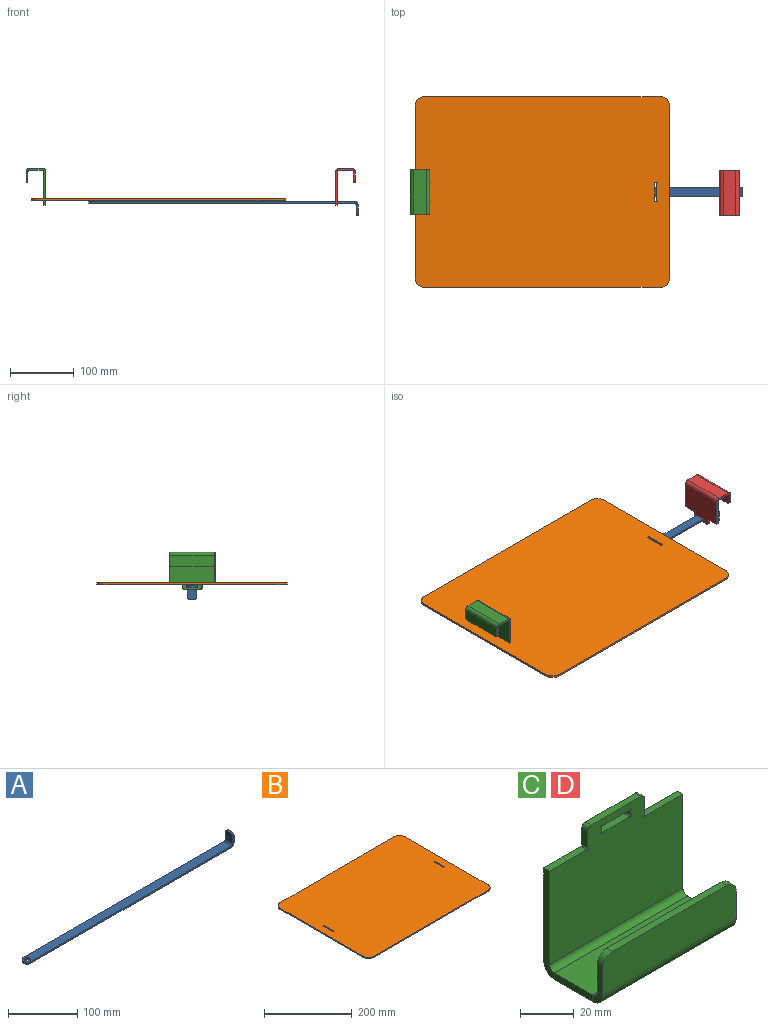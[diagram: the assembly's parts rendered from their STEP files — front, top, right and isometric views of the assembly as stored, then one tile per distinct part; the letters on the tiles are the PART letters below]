
ASSEMBLY  parts=4 mates=6
PART A: 19 faces, bbox 423x15x23 mm
  f0: plane 410.5x3mm, normal (0,1,0), area 1231.5mm2, adj f4,f5,f7,f16
  f1: plane 410.5x3mm, normal (0,-1,0), area 1231.5mm2, adj f4,f5,f6,f15
  f2: cylinder r=4.5mm len=9mm, axis (0,0,-1), area 84.8mm2, adj f4,f5
  f3: plane 3x1mm, normal (-1,0,0), area 3mm2, adj f4,f5,f6,f7
  f4: plane 417.5x15mm, normal (0,0,-1), area 6177.9mm2, adj f0,f1,f2,f3,f6,f7,f17
  f5: plane 417.5x15mm, normal (0,0,1), area 6177.9mm2, adj f0,f1,f2,f3,f6,f7,f18
  f6: cylinder r=7mm len=7mm, axis (0,0,-1), area 33mm2, adj f1,f3,f4,f5
  f7: cylinder r=7mm len=7mm, axis (0,0,1), area 33mm2, adj f0,f3,f4,f5
  f8: plane 12.5x3mm, normal (0,1,0), area 37.5mm2, adj f11,f12,f13,f16
  f9: plane 5x3mm, normal (0,0,1), area 15mm2, adj f11,f12,f13,f14
  f10: plane 12.5x3mm, normal (0,-1,0), area 37.5mm2, adj f11,f12,f14,f15
  f11: plane 17.5x15mm, normal (1,0,0), area 251.8mm2, adj f8,f9,f10,f13,f14,f17
  f12: plane 17.5x15mm, normal (-1,0,0), area 251.8mm2, adj f8,f9,f10,f13,f14,f18
  f13: cylinder r=5mm len=5mm, axis (1,0,0), area 23.6mm2, adj f8,f9,f11,f12
  f14: cylinder r=5mm len=5mm, axis (-1,0,0), area 23.6mm2, adj f9,f10,f11,f12
  f15: plane 5.5x5.5mm, normal (0,-1,0), area 18.8mm2, adj f1,f10,f17,f18
  f16: plane 5.5x5.5mm, normal (0,1,0), area 18.8mm2, adj f0,f8,f17,f18
  f17: cylinder r=5.5mm len=15mm, axis (0,-1,0), area 129.6mm2, adj f4,f11,f15,f16
  f18: cylinder r=2.5mm len=15mm, axis (0,-1,0), area 58.9mm2, adj f5,f12,f15,f16
PART B: 26 faces, bbox 400x300x3 mm
  f0: plane 400x300mm, normal (0,0,1), area 119622.1mm2, adj f2,f3,f4,f5,f6,f7,f8,f9
  f1: plane 400x300mm, normal (0,0,-1), area 119622.1mm2, adj f2,f3,f4,f5,f6,f7,f8,f9
  f2: plane 270x3mm, normal (1,0,0), area 810mm2, adj f0,f1,f6,f9
  f3: plane 370x3mm, normal (0,1,0), area 1110mm2, adj f0,f1,f6,f7
  f4: plane 270x3mm, normal (-1,0,0), area 810mm2, adj f0,f1,f7,f8
  f5: plane 370x3mm, normal (0,-1,0), area 1110mm2, adj f0,f1,f8,f9
  f6: cylinder r=15mm len=15mm, axis (0,0,1), area 70.7mm2, adj f0,f1,f2,f3
  f7: cylinder r=15mm len=15mm, axis (0,0,-1), area 70.7mm2, adj f0,f1,f3,f4
  f8: cylinder r=15mm len=15mm, axis (0,0,1), area 70.7mm2, adj f0,f1,f4,f5
  f9: cylinder r=15mm len=15mm, axis (0,0,-1), area 70.7mm2, adj f0,f1,f2,f5
  f10: plane 3x2mm, normal (0,-1,0), area 6mm2, adj f0,f1,f11,f12
  f11: cylinder r=0.5mm len=3mm, axis (0,0,1), area 7.1mm2, adj f0,f1,f10,f17
  f12: cylinder r=0.5mm len=3mm, axis (0,0,1), area 7.1mm2, adj f0,f1,f10,f13
  f13: plane 29x3mm, normal (1,0,0), area 87mm2, adj f0,f1,f12,f14
  f14: cylinder r=0.5mm len=3mm, axis (0,0,1), area 7.1mm2, adj f0,f1,f13,f15
  f15: plane 3x2mm, normal (0,1,0), area 6mm2, adj f0,f1,f14,f16
  f16: cylinder r=0.5mm len=3mm, axis (0,0,1), area 7.1mm2, adj f0,f1,f15,f17
  f17: plane 29x3mm, normal (-1,0,0), area 87mm2, adj f0,f1,f11,f16
  f18: cylinder r=0.5mm len=3mm, axis (0,0,1), area 7.1mm2, adj f0,f1,f19,f24
  f19: plane 3x2mm, normal (0,-1,0), area 6mm2, adj f0,f1,f18,f20
  f20: cylinder r=0.5mm len=3mm, axis (0,0,1), area 7.1mm2, adj f0,f1,f19,f21
  f21: plane 29x3mm, normal (-1,0,0), area 87mm2, adj f0,f1,f20,f22
  f22: cylinder r=0.5mm len=3mm, axis (0,0,1), area 7.1mm2, adj f0,f1,f21,f23
  f23: plane 3x2mm, normal (0,1,0), area 6mm2, adj f0,f1,f22,f25
  f24: plane 29x3mm, normal (1,0,0), area 87mm2, adj f0,f1,f18,f25
  f25: cylinder r=0.5mm len=3mm, axis (0,0,1), area 7.1mm2, adj f0,f1,f23,f24
PART C: 40 faces, bbox 70x31x58 mm
  f0: plane 12.5x3mm, normal (-1,0,0), area 37.5mm2, adj f3,f4,f6,f37
  f1: plane 12.5x3mm, normal (1,0,0), area 37.5mm2, adj f3,f4,f5,f36
  f2: plane 60x3mm, normal (0,0,1), area 180mm2, adj f3,f4,f5,f6
  f3: plane 70x17.5mm, normal (0,-1,0), area 1214.3mm2, adj f0,f1,f2,f5,f6,f38
  f4: plane 70x17.5mm, normal (0,1,0), area 1214.3mm2, adj f0,f1,f2,f5,f6,f39
  f5: cylinder r=5mm len=5mm, axis (0,-1,0), area 23.6mm2, adj f1,f2,f3,f4
  f6: cylinder r=5mm len=5mm, axis (0,1,0), area 23.6mm2, adj f0,f2,f3,f4
  f7: plane 20x3mm, normal (-1,0,0), area 60mm2, adj f9,f10,f33,f37
  f8: plane 20x3mm, normal (1,0,0), area 60mm2, adj f9,f10,f32,f36
  f9: plane 70x20mm, normal (0,0,-1), area 1400mm2, adj f7,f8,f34,f38
  f10: plane 70x20mm, normal (0,0,1), area 1400mm2, adj f7,f8,f35,f39
  f11: plane 3x2mm, normal (1,0,0), area 6mm2, adj f12,f27,f28,f29
  f12: cylinder r=0.5mm len=3mm, axis (0,1,0), area 7.1mm2, adj f11,f13,f28,f29
  f13: plane 14x3mm, normal (0,0,1), area 42mm2, adj f12,f14,f28,f29
  f14: cylinder r=0.5mm len=3mm, axis (0,1,0), area 7.1mm2, adj f13,f15,f28,f29
  f15: plane 3x2mm, normal (-1,0,0), area 6mm2, adj f14,f16,f28,f29
  f16: cylinder r=0.5mm len=3mm, axis (0,1,0), area 7.1mm2, adj f15,f17,f28,f29
  f17: plane 14x3mm, normal (0,0,-1), area 42mm2, adj f16,f27,f28,f29
  f18: cylinder r=0.5mm len=3mm, axis (0,1,0), area 7.1mm2, adj f19,f26,f28,f29
  f19: plane 19.5x3mm, normal (0,0,1), area 58.5mm2, adj f18,f20,f28,f29
  f20: plane 42.5x3mm, normal (1,0,0), area 127.5mm2, adj f19,f28,f29,f32
  f21: plane 42.5x3mm, normal (-1,0,0), area 127.5mm2, adj f22,f28,f29,f33
  f22: plane 19.5x3mm, normal (0,0,1), area 58.5mm2, adj f21,f23,f28,f29
  f23: cylinder r=0.5mm len=3mm, axis (0,1,0), area 7.1mm2, adj f22,f24,f28,f29
  f24: plane 7.5x3mm, normal (-1,0,0), area 22.5mm2, adj f23,f28,f29,f30
  f25: plane 26x3mm, normal (0,0,1), area 78mm2, adj f28,f29,f30,f31
  f26: plane 7.5x3mm, normal (1,0,0), area 22.5mm2, adj f18,f28,f29,f31
  f27: cylinder r=0.5mm len=3mm, axis (0,1,0), area 7.1mm2, adj f11,f17,f28,f29
  f28: plane 70x52.5mm, normal (0,1,0), area 3224.7mm2, adj f11,f12,f13,f14,f15,f16,f17,f18
  f29: plane 70x52.5mm, normal (0,-1,0), area 3224.7mm2, adj f11,f12,f13,f14,f15,f16,f17,f18
  f30: cylinder r=2mm len=3mm, axis (0,1,0), area 9.4mm2, adj f24,f25,f28,f29
  f31: cylinder r=2mm len=3mm, axis (0,1,0), area 9.4mm2, adj f25,f26,f28,f29
  f32: plane 5.5x5.5mm, normal (1,0,0), area 18.8mm2, adj f8,f20,f34,f35
  f33: plane 5.5x5.5mm, normal (-1,0,0), area 18.8mm2, adj f7,f21,f34,f35
  f34: cylinder r=5.5mm len=70mm, axis (1,0,0), area 604.8mm2, adj f9,f28,f32,f33
  f35: cylinder r=2.5mm len=70mm, axis (1,0,0), area 274.9mm2, adj f10,f29,f32,f33
  f36: plane 5.5x5.5mm, normal (1,0,0), area 18.8mm2, adj f1,f8,f38,f39
  f37: plane 5.5x5.5mm, normal (-1,0,0), area 18.8mm2, adj f0,f7,f38,f39
  f38: cylinder r=5.5mm len=70mm, axis (1,0,0), area 604.8mm2, adj f3,f9,f36,f37
  f39: cylinder r=2.5mm len=70mm, axis (1,0,0), area 274.9mm2, adj f4,f10,f36,f37
PART D: same geometry as C
PLACE A rot(axis=(1,0,0),180deg) t=(-109.16,-7.5,-3.8)mm
PLACE B rot(axis=(1,0,0),180deg) t=(0,0,3)mm
PLACE C rot(axis=(-0.71,-0.71,0),180deg) t=(-205,0,48)mm
PLACE D rot(axis=(0.71,-0.71,0),180deg) t=(306.64,-1.78,48)mm
MATE planar A.f0 <-> C.f11  axis (0,-1,0) through (103.09,-7.5,-2.3)mm
MATE planar C.f29 <-> B.f13  axis (-1,0,0) through (-180,0,22.22)mm
MATE planar C.f26 <-> B.f15  axis (0,1,0) through (-178.5,15,-1.25)mm
MATE planar A.f4 <-> D.f13  axis (0,0,1) through (102.36,0,-0.8)mm
MATE planar D.f19 <-> B.f1  axis (0,0,-1) through (280.14,-27.03,3)mm
MATE planar C.f19 <-> B.f1  axis (0,0,-1) through (-178.5,25.25,3)mm
